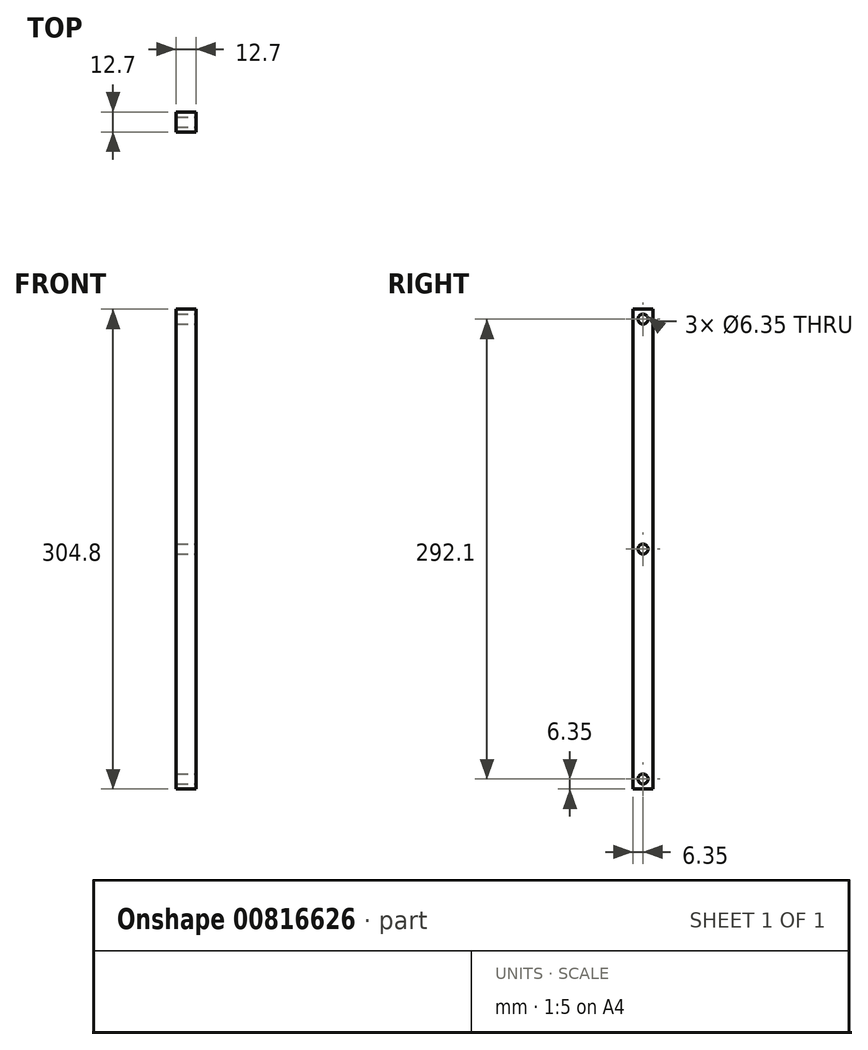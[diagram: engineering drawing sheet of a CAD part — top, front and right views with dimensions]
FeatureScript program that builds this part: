
annotation { "Feature Type Name" : "Feature", "Feature Type Description" : "" }
export const myFeature = defineFeature(function(context is Context, id is Id, definition is map)
    precondition{}
    {
        {
            var Q0;
            Q0=qCreatedBy(makeId("Top.planeOp"),FACE);
            var sketch = newSketch(context, id + "F0", { "sketchPlane" : qUnion([Q0])});
            skLineSegment(sketch, "E0.bottom", {"start": v(6.35, 6.35) * mm, "end": v(-6.35, 6.35) * mm});
            skLineSegment(sketch, "E0.top", {"start": v(6.35, -6.35) * mm, "end": v(-6.35, -6.35) * mm});
            skLineSegment(sketch, "E0.left", {"start": v(6.35, 6.35) * mm, "end": v(6.35, -6.35) * mm});
            skLineSegment(sketch, "E0.right", {"start": v(-6.35, 6.35) * mm, "end": v(-6.35, -6.35) * mm});
            skPoint(sketch, "E0.middle", {"position": v(0, 0) * mm});
            skSolve(sketch);
        }
        {
            var Q0;
            Q0 = qSketchRegion(id + "F0", true);
            extrude(context, id + "F1", {"entities" : qUnion([Q0]), "endBound" : BoundingType.SYMMETRIC, "depth" : 304.8 * mm, "offsetDistance" : 25.4 * mm});
        }
        {
            var Q0;
            Q0=qCreatedBy(makeId("Right.planeOp"),FACE);
            var sketch = newSketch(context, id + "F2", { "sketchPlane" : qUnion([Q0])});
            skCircle(sketch, "E1", {"center": v(0, 146.05) * mm, "radius": 3.18 * mm});
            skCircle(sketch, "E2", {"center": v(0, -146.05) * mm, "radius": 3.18 * mm});
            skCircle(sketch, "E3", {"center": v(0, 0) * mm, "radius": 3.18 * mm});
            skSolve(sketch);
        }
        {
            var Q0;
            Q0 = qSketchRegion(id + "F2", true);
            extrude(context, id + "F3", {"entities" : qUnion([Q0]), "operationType" : NewBodyOperationType.REMOVE, "endBound" : BoundingType.SYMMETRIC, "oppositeDirection" : true, "depth" : 25.4 * mm, "offsetDistance" : 25.4 * mm});
        }
    });
